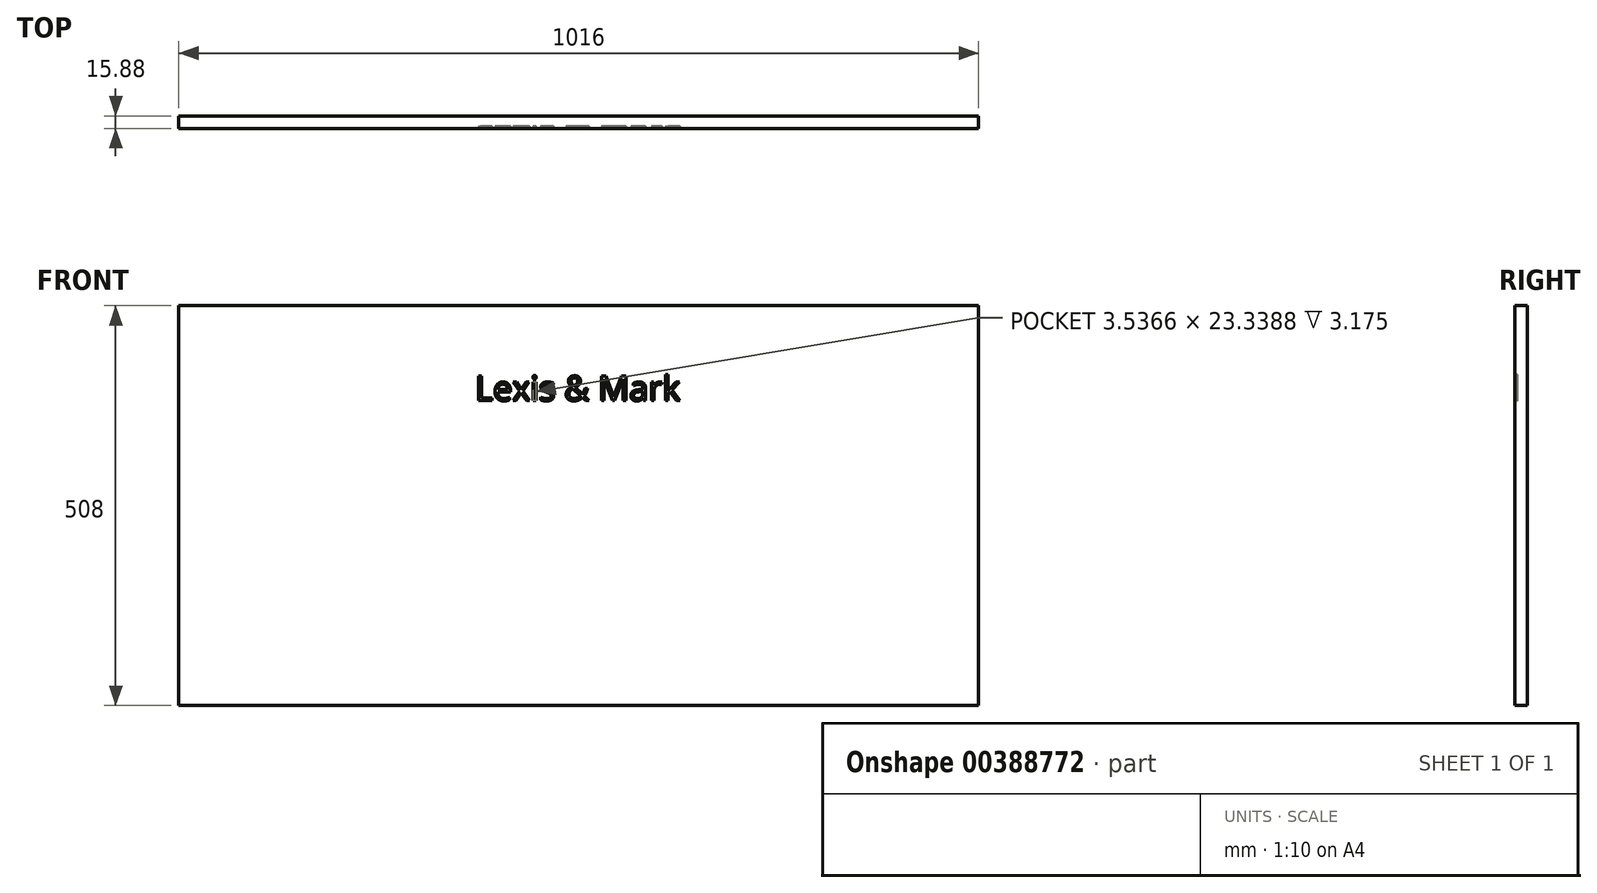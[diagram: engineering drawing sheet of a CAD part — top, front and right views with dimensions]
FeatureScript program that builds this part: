
annotation { "Feature Type Name" : "Feature", "Feature Type Description" : "" }
export const myFeature = defineFeature(function(context is Context, id is Id, definition is map)
    precondition{}
    {
        {
            var Q0;
            Q0=qCreatedBy(makeId("Front.planeOp"),FACE);
            var sketch = newSketch(context, id + "F0", { "sketchPlane" : qUnion([Q0])});
            skLineSegment(sketch, "E0.bottom", {"start": v(508, -254) * mm, "end": v(-508, -254) * mm});
            skLineSegment(sketch, "E0.top", {"start": v(508, 254) * mm, "end": v(-508, 254) * mm});
            skLineSegment(sketch, "E0.left", {"start": v(508, -254) * mm, "end": v(508, 254) * mm});
            skLineSegment(sketch, "E0.right", {"start": v(-508, -254) * mm, "end": v(-508, 254) * mm});
            skPoint(sketch, "E0.middle", {"position": v(0, 0) * mm});
            skSolve(sketch);
        }
        {
            var Q0;
            Q0=makeQuery(id+"F0.imprint","IMPRINT",FACE,{"disambiguationData":[TD([[makeQuery(id+"F0.imprint","IMPRINT",EDGE,{"derivedFrom":sQuery(id+"F0.wireOp",EDGE,"E0.bottom")}),-1.0]])]});
            extrude(context, id + "F1", {"entities" : qUnion([Q0]), "depth" : 15.88 * mm});
        }
        {
            var Q0;
            Q0=makeQuery(id+"F1.opExtrude","CAP_FACE",FACE,{"disambiguationData":[OSD([sQuery(id+"F0.wireOp",EDGE,"E0.bottom"),sQuery(id+"F0.wireOp",EDGE,"E0.top"),sQuery(id+"F0.wireOp",EDGE,"E0.left"),sQuery(id+"F0.wireOp",EDGE,"E0.right")])],"isStart":false});
            var sketch = newSketch(context, id + "F2", { "sketchPlane" : qUnion([Q0])});
            skLineSegment(sketch, "E1", {"start": v(-235.48, 133.32) * mm, "end": v(337.1, 133.32) * mm});
            skText(sketch, "E2", { "text": "Lexis & Mark", "fontName": "OpenSans-Regular.ttf"});
            const initialGuessF2  = {"E2": [-0.1315, 0.13332, 1, 0, 0.0314]};
            skSetInitialGuess(sketch, initialGuessF2);
            skSolve(sketch);
        }
        {
            var Q0;
            Q0 = qSketchRegion(id + "F2", true);
            extrude(context, id + "F3", {"entities" : qUnion([Q0]), "operationType" : NewBodyOperationType.REMOVE, "oppositeDirection" : true, "depth" : 3.17 * mm});
        }
    });
